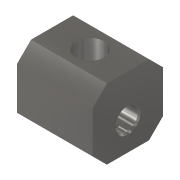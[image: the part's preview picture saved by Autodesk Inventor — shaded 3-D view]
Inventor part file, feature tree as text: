
AUTODESK INVENTOR PART (.ipt)
format: ipt  version: 2018 (Build 220112000, 112)  size: 142,848 bytes
history: native  units: mm
features: sketch x4, hole x3, chamfer x2, extrude x1, projected_geometry x1
ambient origin geometry x8: Origin, YZ Plane, XZ Plane, XY Plane, X Axis, Y Axis, Z Axis, Center Point
bodies: Solid1 (feature_tree)
feature tree (11):
  extrude  "Base"  Depth=50.0mm
  hole  "Hole_Wheel"  [1 undecoded]
  hole  "Hole_Wheel_Fix"  [1 undecoded]
  hole  "ConnectionPipe"  [1 undecoded]
  chamfer  "Chamfer1"  Distance=1.0mm Angle=45.0deg
  chamfer  "Chamfer2"  [1 undecoded]
  sketch  "Sketch1"  dims[d1=50.0mm d2=50.0mm]
  sketch  "Sketch2"  dims[d3=54.0mm d4=0.0mm d5=20.0mm]
  sketch  "Sketch3"  dims[d6=16.0mm d7=6.0mm d8=4.0mm d9=2.0mm d10=90.0deg d11=8.0mm d12=20.594885mm d13=35.0mm]
  projected_geometry  "Projected Loop1"
  sketch  "Sketch4"  dims[d14=4.459mm d15=10.0mm d16=11.5mm d17=3.9mm d18=90.0deg d19=12.8mm d20=20.594885mm d21=20.0mm d22=6.0mm d23=10.0mm d24=3.9mm d25=90.0deg d26=15.0mm d27=20.594885mm d28=10.0mm d29=2.0mm d30=45.0deg d31=1.0mm d32=2.0mm d33=45.0deg]
note: 4 required parameter values undecoded (feature->parameter linkage not recoverable at this tier; creation-order binding heuristic only, values carry confidence <= 0.55)
